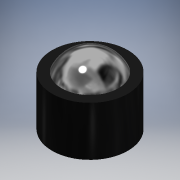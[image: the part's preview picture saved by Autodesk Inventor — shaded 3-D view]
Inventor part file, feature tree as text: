
AUTODESK INVENTOR PART (.ipt)
format: ipt  version: 2019 (Build 230136000, 136)  size: 136,192 bytes
history: native  units: in
note: dims shown in document units (in); Inventor stores cm internally (conversion verified against a paired STEP export)
features: sketch x3, extrude x2, revolve x1
ambient origin geometry x8: Origin, YZ Plane, XZ Plane, XY Plane, X Axis, Y Axis, Z Axis, Center Point
bodies: Solid1 (feature_tree)
feature tree (6):
  extrude  "Extrusion1"  Depth=0.5906in TaperAngle=0.0deg
  revolve  "Revolution1"  [1 undecoded]
  extrude  "Extrusion2"  TaperAngle=90.0deg  [1 undecoded]
  sketch  "Sketch1"  dims[d0=0.9055in d1=0.5906in d2=0.0in]
  sketch  "Sketch2"  dims[d3=0.8071in d4=0.374in]
  sketch  "Sketch3"  dims[d5=180.0deg d6=90.0deg d7=0.2953in d8=0.5906in d9=0.0984in d10=0.0984in d11=0.1969in d12=0.0in]
note: 2 required parameter values undecoded (feature->parameter linkage not recoverable at this tier; creation-order binding heuristic only, values carry confidence <= 0.55)